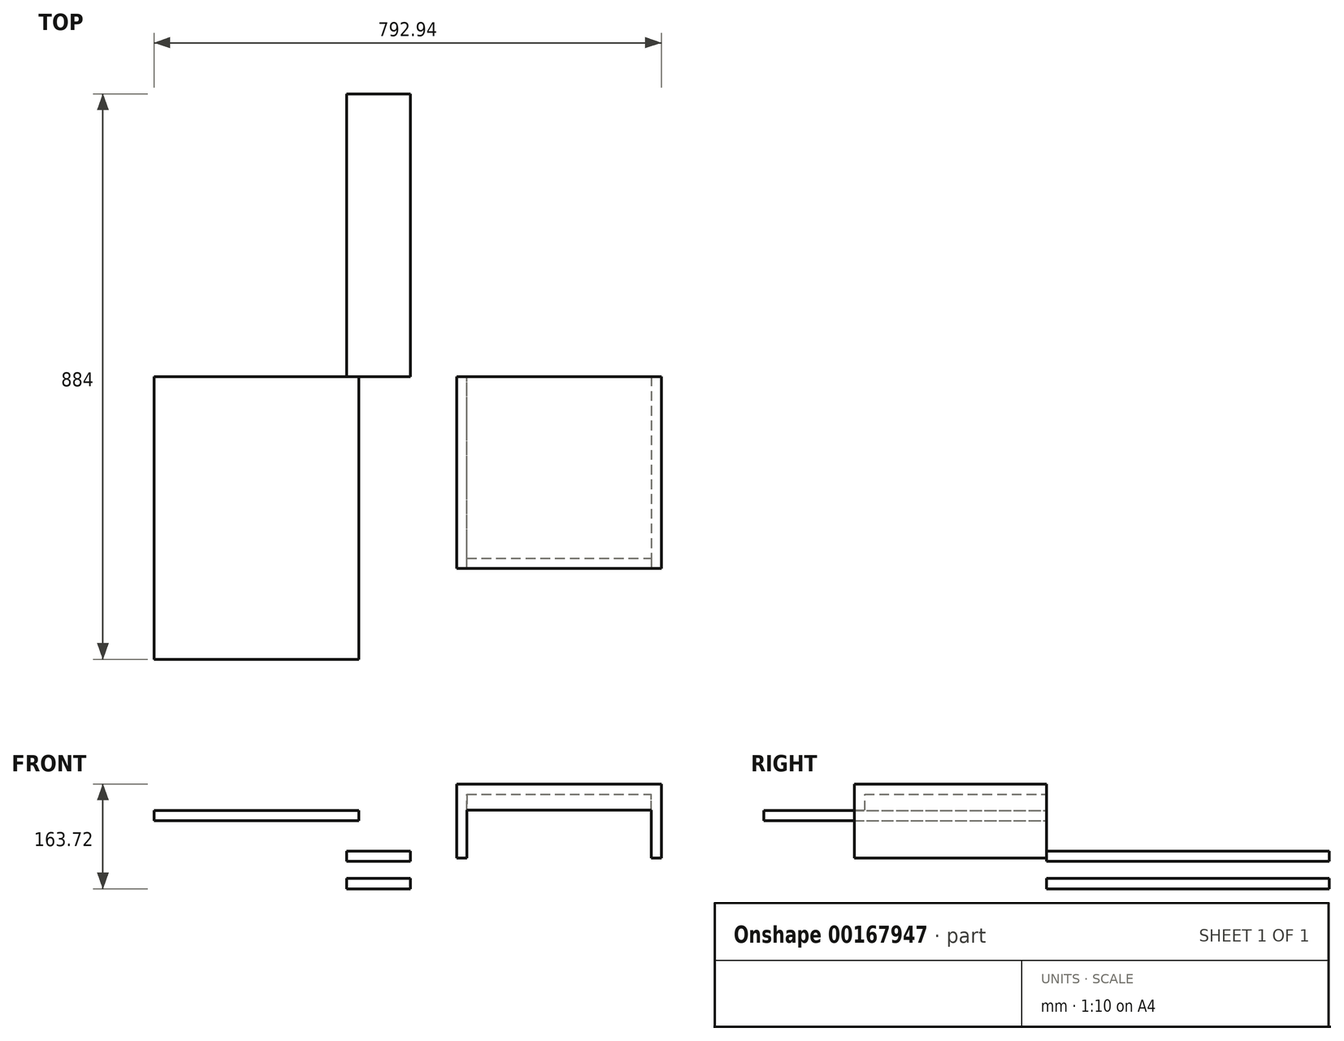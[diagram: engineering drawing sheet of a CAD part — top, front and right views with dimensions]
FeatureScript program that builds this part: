
annotation { "Feature Type Name" : "Feature", "Feature Type Description" : "" }
export const myFeature = defineFeature(function(context is Context, id is Id, definition is map)
    precondition{}
    {
        {
            assignVariable(context, id + "F0", {"name" : "diepte", "anyValue" : 442});
        }
        {
            var Q0;
            Q0=qCreatedBy(makeId("Front.planeOp"),FACE);
            var sketch = newSketch(context, id + "F1", { "sketchPlane" : qUnion([Q0])});
            skLineSegment(sketch, "E0.bottom", {"start": v(0, 0) * mm, "end": v(320, 0) * mm});
            skLineSegment(sketch, "E0.top", {"start": v(0, 16) * mm, "end": v(320, 16) * mm});
            skLineSegment(sketch, "E0.left", {"start": v(0, 0) * mm, "end": v(0, 16) * mm});
            skLineSegment(sketch, "E0.right", {"start": v(320, 0) * mm, "end": v(320, 16) * mm});
            skSolve(sketch);
        }
        {
            var Q0;
            Q0 = qSketchRegion(id + "F1", true);
            extrude(context, id + "F2", {"entities" : qUnion([Q0]), "depth" : 300 * mm});
        }
        {
            var Q0;
            Q0=qCreatedBy(makeId("Front.planeOp"),FACE);
            var sketch = newSketch(context, id + "F3", { "sketchPlane" : qUnion([Q0])});
            skLineSegment(sketch, "E1.bottom", {"start": v(0, 0) * mm, "end": v(16, 0) * mm});
            skLineSegment(sketch, "E1.top", {"start": v(0, -100) * mm, "end": v(16, -100) * mm});
            skLineSegment(sketch, "E1.left", {"start": v(0, 0) * mm, "end": v(0, -100) * mm});
            skLineSegment(sketch, "E1.right", {"start": v(16, 0) * mm, "end": v(16, -100) * mm});
            skSolve(sketch);
        }
        {
            var Q0;
            Q0=makeQuery(id+"F3.imprint","IMPRINT",FACE,{"disambiguationData":[TD([[makeQuery(id+"F3.imprint","IMPRINT",EDGE,{"derivedFrom":sQuery(id+"F3.wireOp",EDGE,"E1.bottom")}),-1.0]])]});
            extrude(context, id + "F4", {"entities" : qUnion([Q0]), "operationType" : NewBodyOperationType.ADD, "depth" : 300 * mm});
        }
        {
            var Q0;
            Q0=makeQuery(id+"F2.opExtrude","SWEPT_FACE",FACE,{"disambiguationData":[OSD([sQuery(id+"F1.wireOp",EDGE,"E0.bottom")])]});
            var sketch = newSketch(context, id + "F5", { "sketchPlane" : qUnion([Q0])});
            skLineSegment(sketch, "E2.bottom", {"start": v(320, 0) * mm, "end": v(304, 0) * mm});
            skLineSegment(sketch, "E2.top", {"start": v(320, 300) * mm, "end": v(304, 300) * mm});
            skLineSegment(sketch, "E2.left", {"start": v(320, 0) * mm, "end": v(320, 300) * mm});
            skLineSegment(sketch, "E2.right", {"start": v(304, 0) * mm, "end": v(304, 300) * mm});
            skSolve(sketch);
        }
        {
            var Q0;
            Q0=makeQuery(id+"F5.imprint","IMPRINT",FACE,{"disambiguationData":[TD([[makeQuery(id+"F5.imprint","IMPRINT",EDGE,{"derivedFrom":sQuery(id+"F5.wireOp",EDGE,"E2.bottom")}),1.0]])]});
            extrude(context, id + "F6", {"entities" : qUnion([Q0]), "operationType" : NewBodyOperationType.ADD, "depth" : 100 * mm});
        }
        {
            var Q0;
            Q0=makeQuery(id+"F2.opExtrude","SWEPT_FACE",FACE,{"disambiguationData":[OSD([sQuery(id+"F1.wireOp",EDGE,"E0.bottom")])]});
            var sketch = newSketch(context, id + "F7", { "sketchPlane" : qUnion([Q0])});
            skLineSegment(sketch, "E3.bottom", {"start": v(16, 300) * mm, "end": v(304, 300) * mm});
            skLineSegment(sketch, "E3.top", {"start": v(16, 284) * mm, "end": v(304, 284) * mm});
            skLineSegment(sketch, "E3.left", {"start": v(16, 300) * mm, "end": v(16, 284) * mm});
            skLineSegment(sketch, "E3.right", {"start": v(304, 300) * mm, "end": v(304, 284) * mm});
            skSolve(sketch);
        }
        {
            var Q0;
            Q0=makeQuery(id+"F7.imprint","IMPRINT",FACE,{"disambiguationData":[TD([[makeQuery(id+"F7.imprint","IMPRINT",EDGE,{"derivedFrom":sQuery(id+"F7.wireOp",EDGE,"E3.bottom")}),-1.0]])]});
            extrude(context, id + "F8", {"entities" : qUnion([Q0]), "operationType" : NewBodyOperationType.ADD, "depth" : 25 * mm});
        }
        {
            var Q0;
            Q0=qCreatedBy(makeId("Front.planeOp"),FACE);
            var sketch = newSketch(context, id + "F9", { "sketchPlane" : qUnion([Q0])});
            skLineSegment(sketch, "E4.bottom", {"start": v(-404.33, 14.38) * mm, "end": v(-84.33, 14.38) * mm});
            skLineSegment(sketch, "E4.top", {"start": v(-404.33, 30.38) * mm, "end": v(-84.33, 30.38) * mm});
            skLineSegment(sketch, "E4.left", {"start": v(-404.33, 14.38) * mm, "end": v(-404.33, 30.38) * mm});
            skLineSegment(sketch, "E4.right", {"start": v(-84.33, 14.38) * mm, "end": v(-84.33, 30.38) * mm});
            skLineSegment(sketch, "E5.bottom", {"start": v(-472.94, -41.45) * mm, "end": v(-152.94, -41.45) * mm});
            skLineSegment(sketch, "E5.top", {"start": v(-472.94, -25.45) * mm, "end": v(-152.94, -25.45) * mm});
            skLineSegment(sketch, "E5.left", {"start": v(-472.94, -41.45) * mm, "end": v(-472.94, -25.45) * mm});
            skLineSegment(sketch, "E5.right", {"start": v(-152.94, -41.45) * mm, "end": v(-152.94, -25.45) * mm});
            skSolve(sketch);
        }
        {
            var Q0;
            Q0=makeQuery(id+"F9.imprint","IMPRINT",FACE,{"disambiguationData":[TD([[makeQuery(id+"F9.imprint","IMPRINT",EDGE,{"derivedFrom":sQuery(id+"F9.wireOp",EDGE,"E5.bottom")}),1.0]])]});
            var Q1;
            Q1=sQuery(id+"F9.wireOp",EDGE,"E5.top");
            var Q2;
            Q2=sQuery(id+"F9.wireOp",EDGE,"E5.left");
            var Q3;
            Q3=sQuery(id+"F9.wireOp",EDGE,"E5.right");
            var Q4;
            Q4=sQuery(id+"F9.wireOp",EDGE,"E5.bottom");
            extrude(context, id + "F10", {"entities" : qUnion([Q0]), "surfaceEntities" : qUnion([Q1, Q2, Q3, Q4]), "depth" : (getVariable(context, 'diepte')) * mm});
        }
        {
            var Q0;
            Q0=makeQuery(id+"F10.opExtrude","CAP_FACE",FACE,{"disambiguationData":[OSD([sQuery(id+"F9.wireOp",EDGE,"E5.bottom"),sQuery(id+"F9.wireOp",EDGE,"E5.top"),sQuery(id+"F9.wireOp",EDGE,"E5.left"),sQuery(id+"F9.wireOp",EDGE,"E5.right")])],"isStart":true});
            var sketch = newSketch(context, id + "F11", { "sketchPlane" : qUnion([Q0])});
            skLineSegment(sketch, "E6.bottom", {"start": v(72.04, -131.72) * mm, "end": v(172.04, -131.72) * mm});
            skLineSegment(sketch, "E6.top", {"start": v(72.04, -147.72) * mm, "end": v(172.04, -147.72) * mm});
            skLineSegment(sketch, "E6.left", {"start": v(72.04, -131.72) * mm, "end": v(72.04, -147.72) * mm});
            skLineSegment(sketch, "E6.right", {"start": v(172.04, -131.72) * mm, "end": v(172.04, -147.72) * mm});
            skSolve(sketch);
        }
        {
            var Q0;
            Q0=makeQuery(id+"F11.imprint","IMPRINT",FACE,{"disambiguationData":[TD([[makeQuery(id+"F11.imprint","IMPRINT",EDGE,{"derivedFrom":sQuery(id+"F11.wireOp",EDGE,"E6.bottom")}),-1.0]])]});
            extrude(context, id + "F12", {"entities" : qUnion([Q0]), "depth" : (getVariable(context, 'diepte')) * mm});
        }
        {
            var Q0;
            Q0=makeQuery(id+"F12.opExtrude","SWEPT_BODY",BODY,{"disambiguationData":[OSD([sQuery(id+"F11.wireOp",EDGE,"E6.bottom"),sQuery(id+"F11.wireOp",EDGE,"E6.top"),sQuery(id+"F11.wireOp",EDGE,"E6.left"),sQuery(id+"F11.wireOp",EDGE,"E6.right")])]});
            transform(context, id + "F13", {"entities" : qUnion([Q0]), "transformType" : TransformType.TRANSLATION_3D, "dx" : 0 * mm, "dy" : 0 * mm, "dz" : 43 * mm, "makeCopy" : true});
        }
    });
